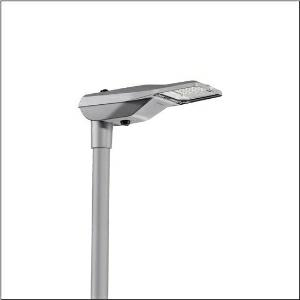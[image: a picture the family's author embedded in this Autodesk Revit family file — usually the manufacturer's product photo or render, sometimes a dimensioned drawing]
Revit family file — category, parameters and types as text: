
# Revit family: streetlight_sl_21_iq_micro___st1_0a_5xe1d41y08db_7ab9
name_source: partatom
category: Lighting Fixtures
units: mm (PartAtom-declared; Revit-internal decimal feet)

## family parameters
Cut with Voids When Loaded = No
Host = Face
Light Source = No
Part Type = Normal
Room Calculation Point = No
Round Connector Dimension = Use Diameter
Shared = No

## types (1)
- --- (1 x LED, 5280 lm, 39.1 W, 4000K)
    Apparent Load = 39 VA
    CIE Flux Codes = 37 72 97 100 100
    Color Rendering = 70
    Color Temperature = 4000K
    Default Elevation = 1800 mm
    Description = Streetlight SL 21 iQ micro, mast luminaire, primary light control with lens, of PMMA, primary optical cover: cover, of toughened safety glass, transparent, light distribution: ST1.0a, light emission: direct distribution, primary light characteristic: asymmetric, installation type: post-top, side-entry, LED, High Power LED, rated luminous flux: 5.280lm, luminous efficacy: 135lm/W, light colour: 740, colour temperature: 4000K, control gear: iQ-Street Remote, D4i with power reduction, control: pre-setting: logarithmic dimming characteristic, Street-Remote, Auto-Match, Temp-Guard, Lumen-Switch, Night-Set, Smart-Wire, Light-Fading, Desk-Remote (wireless, voltage-free reading and setting of iQ features in the workshop via application-optimized NFC function/RFID function), optimised constant luminous flux control (CLO 2.0), mains connection: 220..240V, AC, 50/60Hz, start of lifetime: 39W, end of service life: 41W, reduction: 17W, luminaire housing, of diecast aluminium, powder-coated, Siteco® metallic grey (DB 702S), corrosivity category C5 mid according to DIN EN ISO 12944, please order mast flange separately, inclination adjustable: 0°, 5°, 10°, 15°, sealing non-destructively replaceable, multi-level sealing system, length: 528mm, width: 235mm, height: 110mm, mast flange for spigot size: 42mm (side-entry): 5XC10008XM4, 60/48mm (side-entry/post-top): 5XC10108XM2, 76/60mm (side-entry/post-top): 5XC10108XM1, mounting height: 4..8m, Smart Interface below and above, protection rating (complete): IP66, insulation class (complete): insulation class II (safety insulation), certification: CE, ENEC, ENEC+, VDE, impact resistance: IK10, permissible operating ambient temperature for outdoor applications: -40..+50°C, standard-compliant lighting for roads and squares, packaging unit: 1 piece

Light Distribution: ST1.0a
    Height = 110 mm
    Lamp = 1 x LED
    Lamp Light Flux = 5280 lm
    Lamp Power = 39.1 W
    Lamp count = 1
    Length = 528 mm
    Luminous efficacy = 135 lm/W
    Manufacturer = Siteco
    ModVariant = No
    Model = 5XE1D41Y08DB
    Number of Poles = 1
    OnlyDefault = Yes
    Power Factor = 1
    Product Name = Streetlight SL 21 iQ micro | ST1.0a
    Product group = mast luminaire | pylon top
    ProductGroupID = 6100
    Protection Class = Protection class II
    Protection Degree = IP 66
    RLX_Detail_Level = 1
    RLX_Emergency_Light_Flux = 0 lm
    RLX_Emergency_Type = 0
    RLX_Emergency_Type_DB = No
    RlxData = <blob elided: 98777 chars, md5=3b978a64>
    Socket = socket
    Standby Power = 0 W
    System Light Flux = 5280 lm
    System Power = 39 W
    Type Comments = factory setting: luminous flux: 100 % | dim-lin: 254 | 765 mA
    Type Image = l_1007239.jpg
    URL = http://relux.com
    VarID = @adj_115266
    Voltage = 0 V
    Weight = 0.00 kg
    Width = 235 mm

## geometry (parser evidence)
native form markers: Blend x4, Sweep x11
no freeform markers — native parametric forms only
